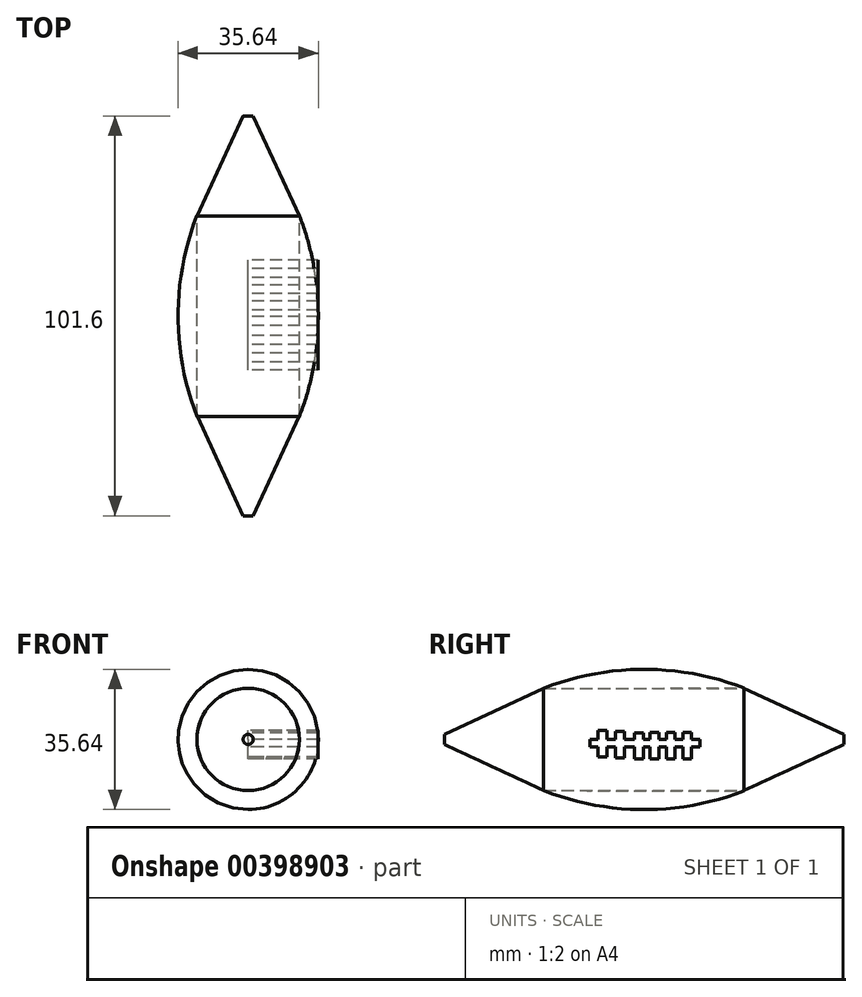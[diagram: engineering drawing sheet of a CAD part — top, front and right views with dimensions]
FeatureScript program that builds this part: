
annotation { "Feature Type Name" : "Feature", "Feature Type Description" : "" }
export const myFeature = defineFeature(function(context is Context, id is Id, definition is map)
    precondition{}
    {
        {
            var Q0;
            Q0=qCreatedBy(makeId("Front.planeOp"),FACE);
            var sketch = newSketch(context, id + "F0", { "sketchPlane" : qUnion([Q0])});
            skCircle(sketch, "E0", {"center": v(0, 0) * mm, "radius": 13 * mm});
            skSolve(sketch);
        }
        {
            var Q0;
            Q0=makeQuery(id+"F0.imprint","IMPRINT",FACE,{"disambiguationData":[TD([[makeQuery(id+"F0.imprint","IMPRINT",EDGE,{"derivedFrom":sQuery(id+"F0.wireOp",EDGE,"E0")}),1.0]])]});
            extrude(context, id + "F1", {"entities" : qUnion([Q0]), "depth" : 25.4 * mm});
        }
        {
            var Q0;
            Q0=makeQuery(id+"F1.opExtrude","CAP_FACE",FACE,{"disambiguationData":[OSD([sQuery(id+"F0.wireOp",EDGE,"E0")])],"isStart":true});
            cPlane(context, id + "F2", {"entities" : qUnion([Q0]), "cplaneType" : CPlaneType.OFFSET, "offset" : 25.4 * mm, "width" : 152.4 * mm, "height" : 152.4 * mm});
        }
        {
            var Q0;
            Q0=qCreatedBy(id+"F2.planeOp",FACE);
            var sketch = newSketch(context, id + "F3", { "sketchPlane" : qUnion([Q0])});
            skCircle(sketch, "E1", {"center": v(0, 0) * mm, "radius": 1.28 * mm});
            skSolve(sketch);
        }
        {
            var Q1;
            Q1=makeQuery(id+"F3.imprint","IMPRINT",FACE,{"disambiguationData":[TD([[makeQuery(id+"F3.imprint","IMPRINT",EDGE,{"derivedFrom":sQuery(id+"F3.wireOp",EDGE,"E1")}),1.0]])]});
            var Q2;
            Q2=makeQuery(id+"F1.opExtrude","CAP_FACE",FACE,{"disambiguationData":[OSD([sQuery(id+"F0.wireOp",EDGE,"E0")])],"isStart":true});
            loft(context, id + "F4", {"operationType" : NewBodyOperationType.ADD, "sheetProfilesArray" : [{ "sheetProfileEntities" : qUnion([Q1]) }, { "sheetProfileEntities" : qUnion([Q2]) }]});
        }
        {
            var Q0;
            Q0=qCreatedBy(makeId("Front.planeOp"),FACE);
            cPlane(context, id + "F5", {"entities" : qUnion([Q0]), "cplaneType" : CPlaneType.OFFSET, "offset" : 25.4 * mm, "width" : 152.4 * mm, "height" : 152.4 * mm});
        }
        {
            var Q0;
            Q0=makeQuery(id+"F1.opExtrude","SWEPT_BODY",BODY,{"disambiguationData":[OSD([sQuery(id+"F0.wireOp",EDGE,"E0")])]});
            var Q1;
            Q1=qCreatedBy(id+"F5.planeOp",FACE);
            mirror(context, id + "F6", {"operationType" : NewBodyOperationType.ADD, "entities" : qUnion([Q0]), "mirrorPlane" : qUnion([Q1])});
        }
        {
            var Q0;
            Q0=qCreatedBy(makeId("Right.planeOp"),FACE);
            var sketch = newSketch(context, id + "F7", { "sketchPlane" : qUnion([Q0])});
            skArc(sketch, "E2", {"start": v(0, 13.04) * mm, "mid": v(-25.5, 17.82) * mm, "end": v(-50.98, 13) * mm});
            skLineSegment(sketch, "E3", {"start": v(0, 13.04) * mm, "end": v(-50.98, 13) * mm});
            skSolve(sketch);
        }
        {
            var Q0;
            Q0=makeQuery(id+"F7.imprint","IMPRINT",FACE,{"disambiguationData":[TD([[makeQuery(id+"F7.imprint","IMPRINT",EDGE,{"derivedFrom":sQuery(id+"F7.wireOp",EDGE,"E2")}),1.0]])]});
            var Q1;
            {var subQ0=makeQuery(id+"F1.opExtrude","SWEPT_FACE",FACE,{"disambiguationData":[OSD([sQuery(id+"F0.wireOp",EDGE,"E0")])]});Q1=makeQuery(id+"F6.boolean.opBoolean","MERGE",FACE,{"derivedFrom":[subQ0,makeQuery(id+"F6.opPattern","COPY",FACE,{"derivedFrom":subQ0,"instanceName":"1"})]});}
            revolve(context, id + "F8", {"entities" : qUnion([Q0]), "axis" : qUnion([Q1]), "revolveType" : RevolveType.FULL});
        }
        {
            var Q0;
            Q0=qCreatedBy(makeId("Right.planeOp"),FACE);
            var sketch = newSketch(context, id + "F9", { "sketchPlane" : qUnion([Q0])});
            skLineSegment(sketch, "E4.bottom", {"start": v(-39.15, 0) * mm, "end": v(-37.12, 0) * mm});
            skLineSegment(sketch, "E4.top", {"start": v(-39.15, -1.96) * mm, "end": v(-37.12, -1.96) * mm});
            skLineSegment(sketch, "E4.left", {"start": v(-39.15, 0) * mm, "end": v(-39.15, -1.96) * mm});
            skLineSegment(sketch, "E4.right", {"start": v(-11.27, 0) * mm, "end": v(-11.27, -1.96) * mm});
            skLineSegment(sketch, "E5.bottom", {"start": v(-37.12, -4.4) * mm, "end": v(-34.88, -4.4) * mm});
            skLineSegment(sketch, "E5.top", {"start": v(-37.12, 2.32) * mm, "end": v(-34.88, 2.32) * mm});
            skLineSegment(sketch, "E5.left", {"start": v(-37.12, -4.4) * mm, "end": v(-37.12, -1.96) * mm});
            skLineSegment(sketch, "E5.right", {"start": v(-34.88, -4.4) * mm, "end": v(-34.88, -1.96) * mm});
            skLineSegment(sketch, "E6.bottom", {"start": v(-27.84, -5) * mm, "end": v(-25.6, -5) * mm});
            skLineSegment(sketch, "E6.top", {"start": v(-27.84, 1.71) * mm, "end": v(-25.6, 1.71) * mm});
            skLineSegment(sketch, "E6.left", {"start": v(-27.84, -5) * mm, "end": v(-27.84, -1.96) * mm});
            skLineSegment(sketch, "E6.right", {"start": v(-25.6, -5) * mm, "end": v(-25.6, -1.96) * mm});
            skLineSegment(sketch, "E7.bottom", {"start": v(-23.88, -4.9) * mm, "end": v(-21.65, -4.9) * mm});
            skLineSegment(sketch, "E7.top", {"start": v(-23.88, 1.81) * mm, "end": v(-21.65, 1.81) * mm});
            skLineSegment(sketch, "E7.left", {"start": v(-23.88, -4.9) * mm, "end": v(-23.88, -1.96) * mm});
            skLineSegment(sketch, "E7.right", {"start": v(-21.65, -4.9) * mm, "end": v(-21.65, -1.96) * mm});
            skLineSegment(sketch, "E8.bottom", {"start": v(-19.78, -4.9) * mm, "end": v(-17.54, -4.9) * mm});
            skLineSegment(sketch, "E8.top", {"start": v(-19.78, 1.81) * mm, "end": v(-17.54, 1.81) * mm});
            skLineSegment(sketch, "E8.left", {"start": v(-19.78, -4.9) * mm, "end": v(-19.78, -1.96) * mm});
            skLineSegment(sketch, "E8.right", {"start": v(-17.54, -4.9) * mm, "end": v(-17.54, -1.96) * mm});
            skLineSegment(sketch, "E9.bottom", {"start": v(-15.6, -4.9) * mm, "end": v(-13.37, -4.9) * mm});
            skLineSegment(sketch, "E9.top", {"start": v(-15.6, 1.81) * mm, "end": v(-13.37, 1.81) * mm});
            skLineSegment(sketch, "E9.left", {"start": v(-15.6, -4.9) * mm, "end": v(-15.6, -1.96) * mm});
            skLineSegment(sketch, "E9.right", {"start": v(-13.37, -4.9) * mm, "end": v(-13.37, -1.96) * mm});
            skLineSegment(sketch, "E10.bottom", {"start": v(-32.66, -4.69) * mm, "end": v(-30.43, -4.69) * mm});
            skLineSegment(sketch, "E10.top", {"start": v(-32.66, 2.03) * mm, "end": v(-30.43, 2.03) * mm});
            skLineSegment(sketch, "E10.left", {"start": v(-32.66, -4.69) * mm, "end": v(-32.66, -1.96) * mm});
            skLineSegment(sketch, "E10.right", {"start": v(-30.43, -4.69) * mm, "end": v(-30.43, -1.96) * mm});
            skLineSegment(sketch, "E11.trimOffspring", {"start": v(-30.43, 0) * mm, "end": v(-27.84, 0) * mm});
            skLineSegment(sketch, "E12.trimOffspring", {"start": v(-34.88, 0) * mm, "end": v(-32.66, 0) * mm});
            skLineSegment(sketch, "E13.trimOffspring", {"start": v(-25.6, 0) * mm, "end": v(-23.88, 0) * mm});
            skLineSegment(sketch, "E14.trimOffspring", {"start": v(-21.65, 0) * mm, "end": v(-19.78, 0) * mm});
            skLineSegment(sketch, "E15.trimOffspring", {"start": v(-17.54, 0) * mm, "end": v(-15.6, 0) * mm});
            skLineSegment(sketch, "E16.trimOffspring", {"start": v(-13.37, 0) * mm, "end": v(-11.27, 0) * mm});
            skLineSegment(sketch, "E17.trimOffspring", {"start": v(-13.37, 0) * mm, "end": v(-13.37, 1.81) * mm});
            skLineSegment(sketch, "E18.trimOffspring", {"start": v(-17.54, 0) * mm, "end": v(-17.54, 1.81) * mm});
            skLineSegment(sketch, "E19.trimOffspring", {"start": v(-15.6, 0) * mm, "end": v(-15.6, 1.81) * mm});
            skLineSegment(sketch, "E20.trimOffspring", {"start": v(-13.37, -1.96) * mm, "end": v(-11.27, -1.96) * mm});
            skLineSegment(sketch, "E21.trimOffspring", {"start": v(-17.54, -1.96) * mm, "end": v(-15.6, -1.96) * mm});
            skLineSegment(sketch, "E22.trimOffspring", {"start": v(-19.78, 0) * mm, "end": v(-19.78, 1.81) * mm});
            skLineSegment(sketch, "E23.trimOffspring", {"start": v(-21.65, 0) * mm, "end": v(-21.65, 1.81) * mm});
            skLineSegment(sketch, "E24.trimOffspring", {"start": v(-23.88, 0) * mm, "end": v(-23.88, 1.81) * mm});
            skLineSegment(sketch, "E25.trimOffspring", {"start": v(-25.6, 0) * mm, "end": v(-25.6, 1.71) * mm});
            skLineSegment(sketch, "E26.trimOffspring", {"start": v(-27.84, 0) * mm, "end": v(-27.84, 1.71) * mm});
            skLineSegment(sketch, "E27.trimOffspring", {"start": v(-30.43, 0) * mm, "end": v(-30.43, 2.03) * mm});
            skLineSegment(sketch, "E28.trimOffspring", {"start": v(-32.66, 0) * mm, "end": v(-32.66, 2.03) * mm});
            skLineSegment(sketch, "E29.trimOffspring", {"start": v(-34.88, -1.96) * mm, "end": v(-32.66, -1.96) * mm});
            skLineSegment(sketch, "E30.trimOffspring", {"start": v(-25.6, -1.96) * mm, "end": v(-19.78, -1.96) * mm});
            skLineSegment(sketch, "E31.trimOffspring", {"start": v(-34.88, 0) * mm, "end": v(-34.88, 2.32) * mm});
            skLineSegment(sketch, "E32.trimOffspring", {"start": v(-37.12, 0) * mm, "end": v(-37.12, 2.32) * mm});
            skLineSegment(sketch, "E33", {"start": v(-27.84, -1.96) * mm, "end": v(-30.43, -1.96) * mm});
            skSolve(sketch);
        }
        {
            var Q0;
            Q0 = qSketchRegion(id + "F9", true);
            extrude(context, id + "F10", {"entities" : qUnion([Q0]), "depth" : 17.78 * mm});
        }
    });
